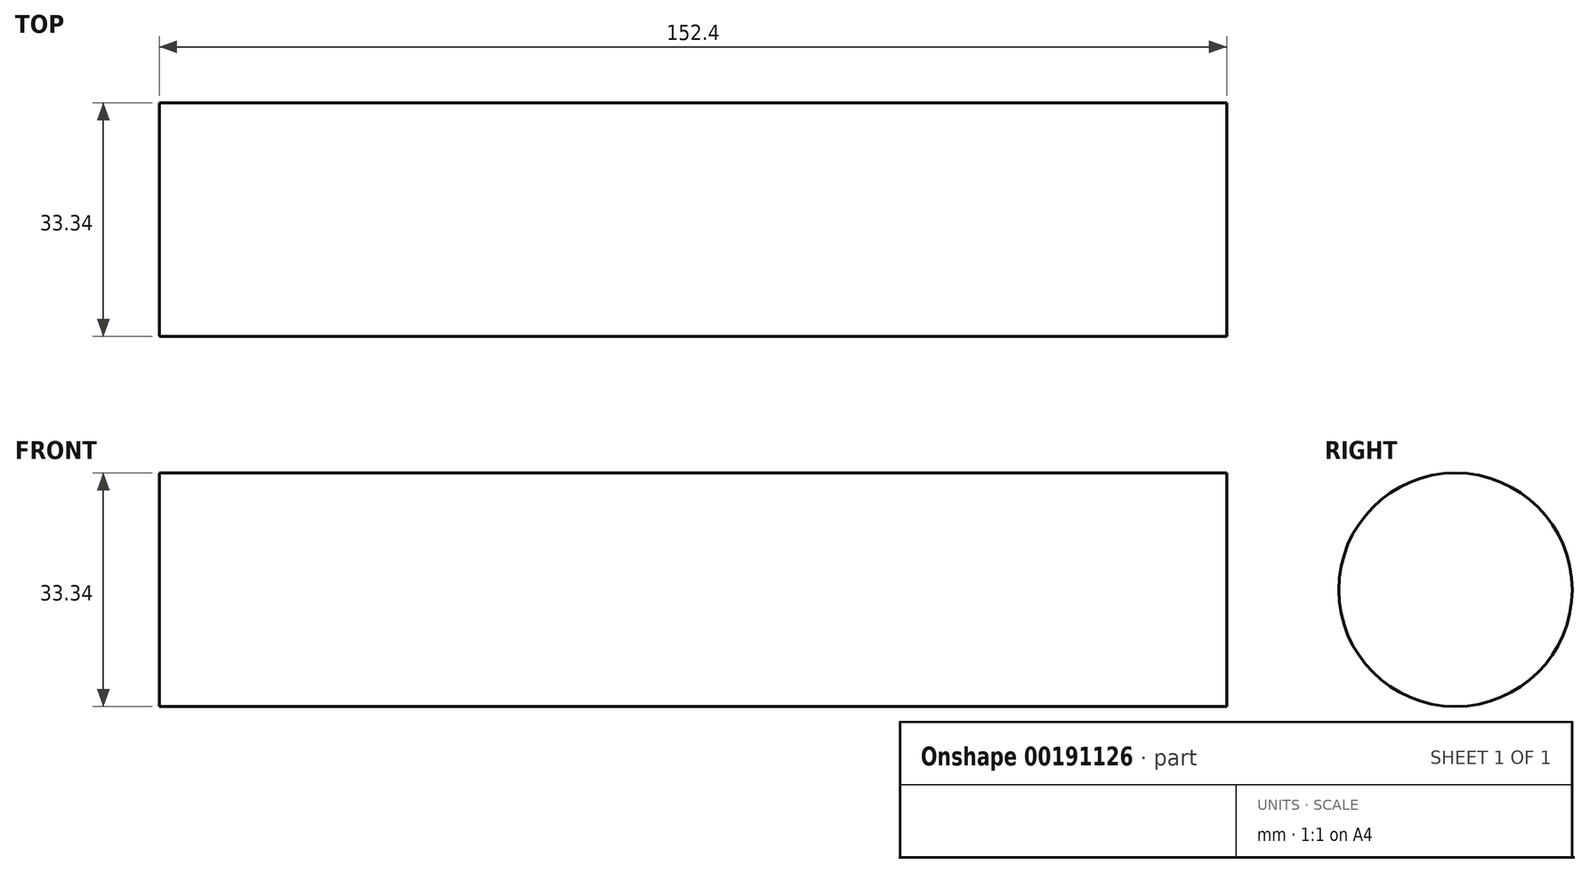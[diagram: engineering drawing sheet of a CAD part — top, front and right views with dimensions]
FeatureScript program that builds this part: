
annotation { "Feature Type Name" : "Feature", "Feature Type Description" : "" }
export const myFeature = defineFeature(function(context is Context, id is Id, definition is map)
    precondition{}
    {
        {
            var Q0;
            Q0=qCreatedBy(makeId("Right.planeOp"),FACE);
            var sketch = newSketch(context, id + "F0", { "sketchPlane" : qUnion([Q0])});
            skCircle(sketch, "E0", {"center": v(0, 0) * mm, "radius": 16.67 * mm});
            skSolve(sketch);
        }
        {
            var Q0;
            Q0=makeQuery(id+"F0.imprint","IMPRINT",FACE,{"disambiguationData":[TD([[makeQuery(id+"F0.imprint","IMPRINT",EDGE,{"derivedFrom":sQuery(id+"F0.wireOp",EDGE,"E0")}),1.0]])]});
            extrude(context, id + "F1", {"entities" : qUnion([Q0]), "depth" : 152.4 * mm});
        }
    });
